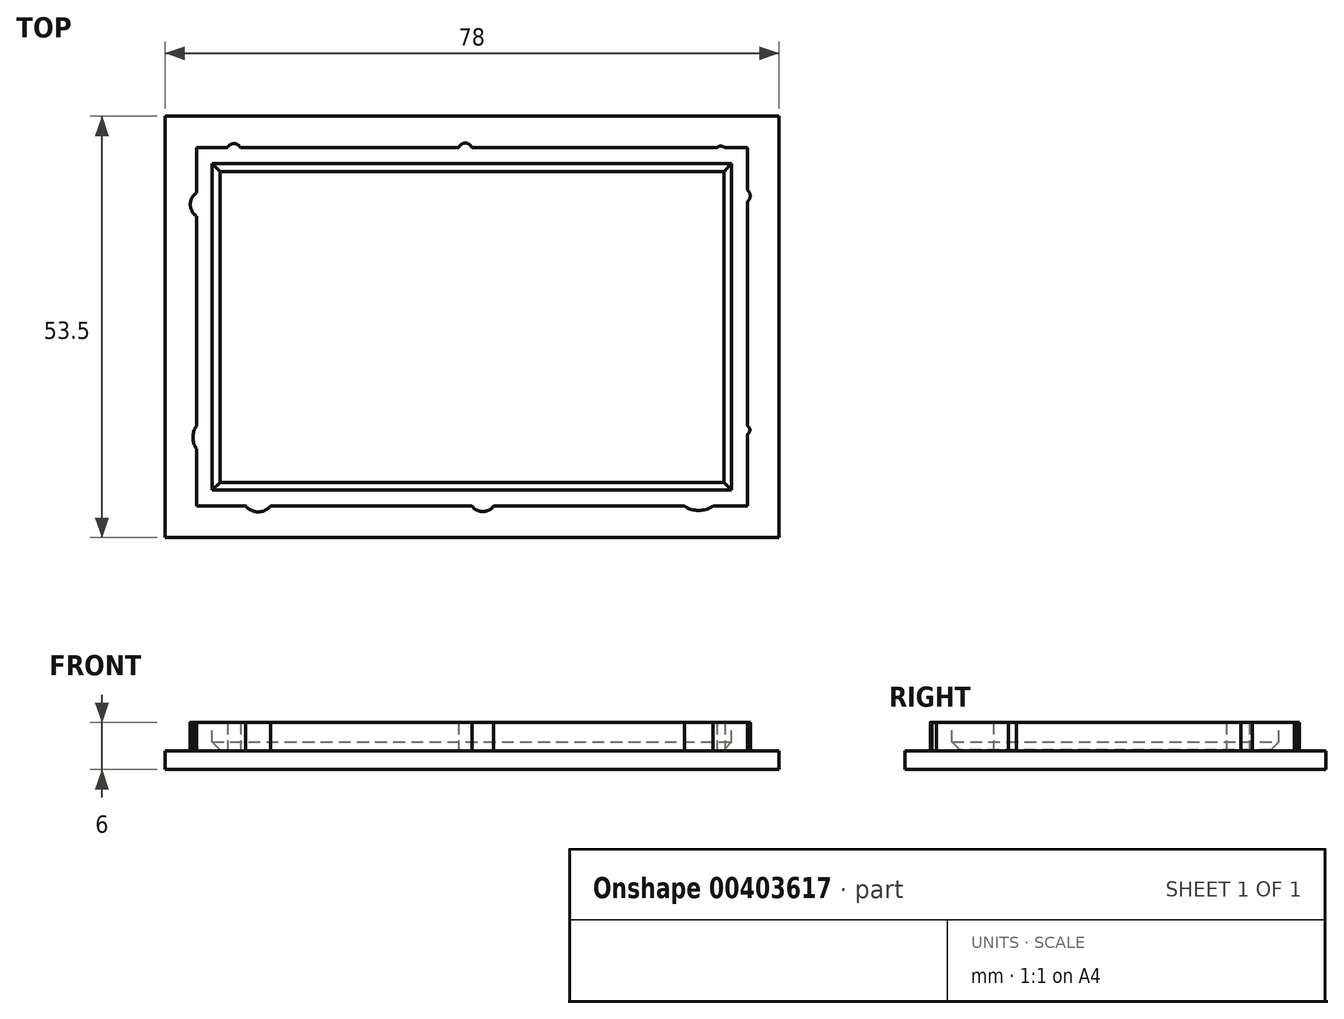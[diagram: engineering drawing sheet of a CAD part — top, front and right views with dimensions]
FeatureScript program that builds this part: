
annotation { "Feature Type Name" : "Feature", "Feature Type Description" : "" }
export const myFeature = defineFeature(function(context is Context, id is Id, definition is map)
    precondition{}
    {
        {
            var Q0;
            Q0=qCreatedBy(makeId("Top.planeOp"),FACE);
            var sketch = newSketch(context, id + "F0", { "sketchPlane" : qUnion([Q0])});
            skLineSegment(sketch, "E0.bottom", {"start": v(-10.94, -3.04) * mm, "end": v(-7, -3.04) * mm});
            skLineSegment(sketch, "E0.top", {"start": v(-10.94, -48.54) * mm, "end": v(-4.66, -48.54) * mm});
            skLineSegment(sketch, "E0.left", {"start": v(-10.94, -3.04) * mm, "end": v(-10.94, -8.78) * mm});
            skLineSegment(sketch, "E0.right", {"start": v(59.06, -3.04) * mm, "end": v(59.06, -8.43) * mm});
            skLineSegment(sketch, "E1.bottom", {"start": v(-14.94, -52.54) * mm, "end": v(63.06, -52.54) * mm});
            skLineSegment(sketch, "E1.top", {"start": v(-14.94, 0.96) * mm, "end": v(63.06, 0.96) * mm});
            skLineSegment(sketch, "E1.left", {"start": v(-14.94, -52.54) * mm, "end": v(-14.94, 0.96) * mm});
            skLineSegment(sketch, "E1.right", {"start": v(63.06, -52.54) * mm, "end": v(63.06, 0.96) * mm});
            skArc(sketch, "E2", {"start": v(24.06, -3.04) * mm, "mid": v(23.22, -2.45) * mm, "end": v(22.38, -3.04) * mm});
            skArc(sketch, "E3", {"start": v(-5.35, -3.04) * mm, "mid": v(-6.17, -2.5) * mm, "end": v(-7, -3.04) * mm});
            skArc(sketch, "E4", {"start": v(56.2, -3.04) * mm, "mid": v(55.68, -2.83) * mm, "end": v(55.16, -3.04) * mm});
            skArc(sketch, "E5", {"start": v(59.06, -9.87) * mm, "mid": v(59.42, -9.15) * mm, "end": v(59.06, -8.43) * mm});
            skArc(sketch, "E6", {"start": v(59.06, -39.42) * mm, "mid": v(59.36, -38.9) * mm, "end": v(59.06, -38.37) * mm});
            skArc(sketch, "E7", {"start": v(51.04, -48.54) * mm, "mid": v(52.86, -49.12) * mm, "end": v(54.67, -48.54) * mm});
            skArc(sketch, "E8", {"start": v(24.06, -48.54) * mm, "mid": v(25.44, -49.26) * mm, "end": v(26.82, -48.54) * mm});
            skArc(sketch, "E9", {"start": v(-4.66, -48.54) * mm, "mid": v(-3.1, -49.3) * mm, "end": v(-1.53, -48.54) * mm});
            skArc(sketch, "E10", {"start": v(-10.94, -38.37) * mm, "mid": v(-11.39, -39.83) * mm, "end": v(-10.94, -41.29) * mm});
            skArc(sketch, "E11", {"start": v(-10.94, -8.78) * mm, "mid": v(-11.71, -10.25) * mm, "end": v(-10.94, -11.72) * mm});
            skLineSegment(sketch, "E12.trimOffspring", {"start": v(-10.94, -11.72) * mm, "end": v(-10.94, -38.37) * mm});
            skLineSegment(sketch, "E13.trimOffspring", {"start": v(-10.94, -41.29) * mm, "end": v(-10.94, -48.54) * mm});
            skLineSegment(sketch, "E14.trimOffspring", {"start": v(-5.35, -3.04) * mm, "end": v(22.38, -3.04) * mm});
            skLineSegment(sketch, "E15.trimOffspring", {"start": v(24.06, -3.04) * mm, "end": v(55.16, -3.04) * mm});
            skLineSegment(sketch, "E16.trimOffspring", {"start": v(-1.53, -48.54) * mm, "end": v(24.06, -48.54) * mm});
            skLineSegment(sketch, "E17.trimOffspring", {"start": v(26.82, -48.54) * mm, "end": v(51.04, -48.54) * mm});
            skLineSegment(sketch, "E18.trimOffspring", {"start": v(54.67, -48.54) * mm, "end": v(59.06, -48.54) * mm});
            skLineSegment(sketch, "E19.trimOffspring", {"start": v(59.06, -39.42) * mm, "end": v(59.06, -48.54) * mm});
            skLineSegment(sketch, "E20.trimOffspring", {"start": v(59.06, -9.87) * mm, "end": v(59.06, -38.37) * mm});
            skLineSegment(sketch, "E21.trimOffspring", {"start": v(56.2, -3.04) * mm, "end": v(59.06, -3.04) * mm});
            skSolve(sketch);
        }
        {
            var Q0;
            Q0 = qSketchRegion(id + "F0", true);
            extrude(context, id + "F1", {"entities" : qUnion([Q0]), "depth" : 2.4 * mm});
        }
        {
            var Q0;
            Q0=makeQuery(id+"F0.imprint","IMPRINT",FACE,{"disambiguationData":[TD([[makeQuery(id+"F0.imprint","IMPRINT",EDGE,{"derivedFrom":sQuery(id+"F0.wireOp",EDGE,"E0.bottom")}),-1.0]])]});
            extrude(context, id + "F2", {"entities" : qUnion([Q0]), "operationType" : NewBodyOperationType.ADD, "depth" : 6 * mm});
        }
        {
            var Q0;
            Q0=makeQuery(id+"F2.opExtrude","CAP_FACE",FACE,{"disambiguationData":[OSD([sQuery(id+"F0.wireOp",EDGE,"E0.bottom"),sQuery(id+"F0.wireOp",EDGE,"E0.top"),sQuery(id+"F0.wireOp",EDGE,"E0.left"),sQuery(id+"F0.wireOp",EDGE,"E0.right")])],"isStart":false});
            var sketch = newSketch(context, id + "F3", { "sketchPlane" : qUnion([Q0])});
            skLineSegment(sketch, "E22.bottom", {"start": v(-8.94, -5.04) * mm, "end": v(57.06, -5.04) * mm});
            skLineSegment(sketch, "E22.top", {"start": v(-8.94, -46.54) * mm, "end": v(57.06, -46.54) * mm});
            skLineSegment(sketch, "E22.left", {"start": v(-8.94, -5.04) * mm, "end": v(-8.94, -46.54) * mm});
            skLineSegment(sketch, "E22.right", {"start": v(57.06, -5.04) * mm, "end": v(57.06, -46.54) * mm});
            skSolve(sketch);
        }
        {
            var Q0;
            Q0=makeQuery(id+"F3.imprint","IMPRINT",FACE,{"disambiguationData":[TD([[makeQuery(id+"F3.imprint","IMPRINT",EDGE,{"derivedFrom":sQuery(id+"F3.wireOp",EDGE,"E22.bottom")}),-1.0]])]});
            extrude(context, id + "F4", {"entities" : qUnion([Q0]), "operationType" : NewBodyOperationType.REMOVE, "oppositeDirection" : true, "depth" : 3.5 * mm});
        }
        {
            var Q0;
            Q0=makeQuery(id+"F4.boolean.opBoolean","COPY",EDGE,{"derivedFrom":makeQuery(id+"F4.opExtrude","CAP_EDGE",EDGE,{"disambiguationData":[OSD([sQuery(id+"F3.wireOp",EDGE,"E22.left")])],"isStart":false})});
            var Q1;
            Q1=makeQuery(id+"F4.boolean.opBoolean","COPY",EDGE,{"derivedFrom":makeQuery(id+"F4.opExtrude","CAP_EDGE",EDGE,{"disambiguationData":[OSD([sQuery(id+"F3.wireOp",EDGE,"E22.bottom")])],"isStart":false})});
            var Q2;
            Q2=makeQuery(id+"F4.boolean.opBoolean","COPY",EDGE,{"derivedFrom":makeQuery(id+"F4.opExtrude","CAP_EDGE",EDGE,{"disambiguationData":[OSD([sQuery(id+"F3.wireOp",EDGE,"E22.right")])],"isStart":false})});
            var Q3;
            Q3=makeQuery(id+"F4.boolean.opBoolean","COPY",EDGE,{"derivedFrom":makeQuery(id+"F4.opExtrude","CAP_EDGE",EDGE,{"disambiguationData":[OSD([sQuery(id+"F3.wireOp",EDGE,"E22.top")])],"isStart":false})});
            chamfer(context, id + "F5", {"entities" : qUnion([Q0, Q1, Q2, Q3]), "width" : 1 * mm, "tangentPropagation" : true});
        }
    });
